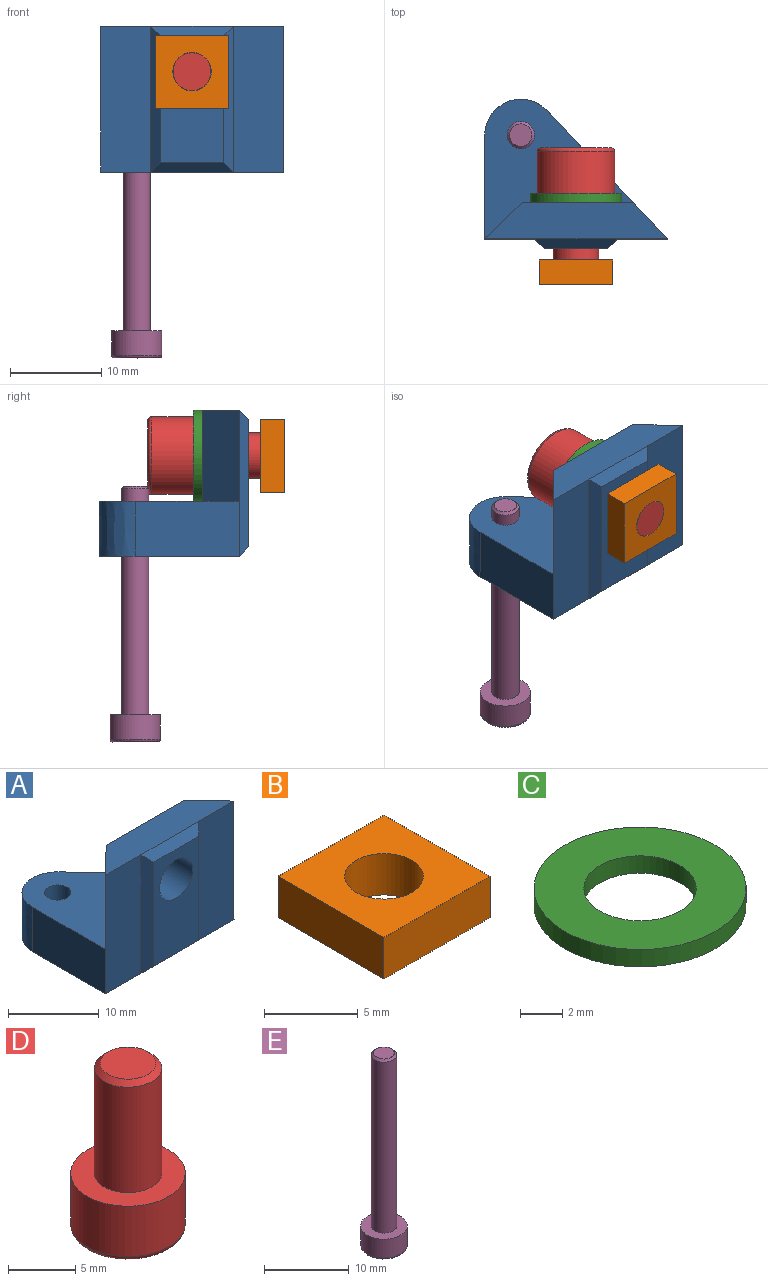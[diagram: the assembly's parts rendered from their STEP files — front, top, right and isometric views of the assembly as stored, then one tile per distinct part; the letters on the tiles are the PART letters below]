
ASSEMBLY  parts=5 mates=4
PART A: 17 faces, bbox 20.7x24.5x233.1 mm
  f0: plane 20.47x15.79mm, normal (0,0,-1), area 186.1mm2, adj f4,f7,f8,f12,f13,f14,f15
  f1: plane 12.17x10mm, normal (0,1,0), area 100.4mm2, adj f2,f3,f4,f5,f16
  f2: plane 10x4.09mm, normal (-0.7,0.72,0), area 57.2mm2, adj f1,f3,f5,f8
  f3: plane 16.73x15.8mm, normal (0,0,1), area 122mm2, adj f1,f2,f4,f13,f14,f15
  f4: plane 16x14.07mm, normal (0.73,0.68,0), area 170.4mm2, adj f0,f1,f3,f5,f7,f15
  f5: plane 20x4mm, normal (0,0,1), area 64.3mm2, adj f1,f2,f4,f6,f7,f8
  f6: plane 9x1mm, normal (0,-0.71,0.71), area 11.3mm2, adj f5,f9,f10,f11
  f7: plane 16x5.5mm, normal (0,-1,0), area 88mm2, adj f0,f4,f5,f9
  f8: plane 16x5.5mm, normal (0,-1,0), area 88mm2, adj f0,f2,f5,f11,f13
  f9: plane 16x1mm, normal (0.71,-0.71,0), area 21.2mm2, adj f6,f7,f10,f12
  f10: plane 14x7mm, normal (0,-1,0), area 76.8mm2, adj f6,f9,f11,f12,f16
  f11: plane 16x1mm, normal (-0.71,-0.71,0), area 21.2mm2, adj f6,f8,f10,f12
  f12: plane 9x1mm, normal (0,-0.71,-0.71), area 11.3mm2, adj f0,f9,f10,f11
  f13: cylinder r=3770.31mm len=16.32mm, axis (0,-0.88,-0.47), area 68.4mm2, adj f0,f3,f8,f15
  f14: cylinder r=1.45mm len=6mm, axis (0,0,1), area 54.7mm2, adj f0,f3
  f15: bspline ~232.63x11.76mm, area 56.6mm2, adj f0,f3,f4,f13
  f16: cylinder r=2.6mm len=5.2mm, axis (0,-1,0), area 81.7mm2, adj f1,f10
PART B: 7 faces, bbox 8x8x2.7 mm
  f0: plane 8x2.7mm, normal (0,-1,0), area 21.6mm2, adj f1,f4,f5,f6
  f1: plane 8x2.7mm, normal (1,0,0), area 21.6mm2, adj f0,f2,f5,f6
  f2: plane 8x2.7mm, normal (0,1,0), area 21.6mm2, adj f1,f4,f5,f6
  f3: cylinder r=2.1mm len=4.2mm, axis (0,0,-1), area 35.6mm2, adj f5,f6
  f4: plane 8x2.7mm, normal (-1,0,0), area 21.6mm2, adj f0,f2,f5,f6
  f5: plane 8x8mm, normal (0,0,1), area 50.1mm2, adj f0,f1,f2,f3,f4
  f6: plane 8x8mm, normal (0,0,-1), area 50.1mm2, adj f0,f1,f2,f3,f4
PART C: 4 faces, bbox 10x10x1 mm
  f0: cylinder r=2.65mm len=5.3mm, axis (0,0,-1), area 16.7mm2, adj f2,f3
  f1: cylinder r=5mm len=10mm, axis (0,0,-1), area 31.4mm2, adj f2,f3
  f2: plane 10x10mm, normal (0,0,1), area 56.5mm2, adj f0,f1
  f3: plane 10x10mm, normal (0,0,-1), area 56.5mm2, adj f0,f1
PART D: 14 faces, bbox 9.2x9.2x15 mm
  f0: plane 7.65x7.65mm, normal (0,0,-1), area 31.4mm2, adj f3,f4,f5,f6,f7,f8,f9
  f1: cylinder r=4.25mm len=8.5mm, axis (0,0,1), area 122.2mm2, adj f2,f3
  f2: plane 8.5x8.5mm, normal (0,0,1), area 37.1mm2, adj f1,f11
  f3: torus R=3.82mm, axis (0,0,-1), area 17.2mm2, adj f0,f1
  f4: plane 2.5x2.36mm, normal (-1,0,0), area 5.9mm2, adj f0,f5,f9,f10
  f5: plane 2.5x2.05mm, normal (-0.5,-0.87,0), area 5.9mm2, adj f0,f4,f6,f10
  f6: plane 2.5x2.05mm, normal (0.5,-0.87,0), area 5.9mm2, adj f0,f5,f7,f10
  f7: plane 2.5x2.36mm, normal (1,0,0), area 5.9mm2, adj f0,f6,f8,f10
  f8: plane 2.5x2.05mm, normal (0.5,0.87,0), area 5.9mm2, adj f0,f7,f9,f10
  f9: plane 2.5x2.05mm, normal (-0.5,0.87,0), area 5.9mm2, adj f0,f4,f8,f10
  f10: plane 4.73x4.1mm, normal (0,0,-1), area 14.5mm2, adj f4,f5,f6,f7,f8,f9
  f11: cylinder r=2.5mm len=9.57mm, axis (0,0,-1), area 150.3mm2, adj f2,f13
  f12: plane 4.13x4.13mm, normal (0,0,1), area 13.4mm2, adj f13
  f13: cone r=2.07mm half-angle=45deg, axis (0,0,-1), area 8.8mm2, adj f11,f12
PART E: 14 faces, bbox 6x6x28 mm
  f0: plane 4.95x4.95mm, normal (0,0,-1), area 13.5mm2, adj f3,f4,f5,f6,f7,f8,f9
  f1: cylinder r=2.75mm len=5.5mm, axis (0,0,1), area 47.1mm2, adj f2,f3
  f2: plane 5.5x5.5mm, normal (0,0,1), area 16.7mm2, adj f1,f11
  f3: torus R=2.48mm, axis (0,0,-1), area 7.2mm2, adj f0,f1
  f4: plane 1.5x1.49mm, normal (-1,0,0), area 2.2mm2, adj f0,f5,f9,f10
  f5: plane 1.5x1.29mm, normal (-0.5,-0.87,0), area 2.2mm2, adj f0,f4,f6,f10
  f6: plane 1.5x1.29mm, normal (0.5,-0.87,0), area 2.2mm2, adj f0,f5,f7,f10
  f7: plane 1.5x1.49mm, normal (1,0,0), area 2.2mm2, adj f0,f6,f8,f10
  f8: plane 1.5x1.29mm, normal (0.5,0.87,0), area 2.2mm2, adj f0,f7,f9,f10
  f9: plane 1.5x1.29mm, normal (-0.5,0.87,0), area 2.2mm2, adj f0,f4,f8,f10
  f10: plane 2.98x2.58mm, normal (0,0,-1), area 5.8mm2, adj f4,f5,f6,f7,f8,f9
  f11: cylinder r=1.5mm len=24.73mm, axis (0,0,-1), area 233.1mm2, adj f2,f13
  f12: plane 2.46x2.46mm, normal (0,0,1), area 4.7mm2, adj f13
  f13: cone r=1.23mm half-angle=45deg, axis (0,0,-1), area 3.3mm2, adj f11,f12
PLACE A t=(0.33,-0.12,8.3)mm fixed
PLACE B rot(axis=(1,0,0),90deg) t=(12.48,0.35,19.3)mm
PLACE C rot(axis=(1,0,0),90deg) t=(12.48,7.65,19.3)mm
PLACE D rot(axis=(1,0,0),90deg) t=(12.48,7.65,19.3)mm
PLACE E rot(axis=(-0.65,0,0.76),0deg) t=(6.42,14.04,-9.06)mm
MATE fastened D.f1 <-> C.f0  axis (0,-1,0) through (12.48,7.65,19.3)mm
MATE fastened B.f3 <-> D.f1  axis (0,-1,0) through (12.48,-2.35,19.3)mm
MATE slider E.f1 <-> A.f14  axis (0,0,-1) through (6.42,14.04,3.3)mm
MATE fastened C.f0 <-> A.f16  axis (0,-1,0) through (12.48,6.65,19.3)mm
